# Revit family: HVAC_PTAC-Heat-Pump
name_source: partatom
category: Mechanical Equipment
units: mm (PartAtom-declared; Revit-internal decimal feet)

## family parameters
Classification Number = 23.75.70.21.21
Cut with Voids When Loaded = No
Host = Face
Maintain Annotation Orientation = No
Part Type = Normal
Room Calculation Point = No
Round Connector Dimension = Use Diameter
Shared = No

## types (2) — shared parameters
Assembly Code = D3050200
Cooling EER = 13
Default Elevation = 0' - 0"
Dehumidification Rate = 1.7 pts / hr
Electrical_Amperage = 0 A
Electrical_Frequency = 0 Hz
Electrical_Phase = 1
Heating = Yes
Heating COP = 4
Indoor Fan CFM = 250 - 409 CFM
Keynote = 23 81 00
Poles = 2
Power Factor = 0.96
SHR = 0.79
STC Rating = 29
Standards Conformance = UL  ;  ULc  ;  AHRI
Temperature Range = 60 - 85 F
Unit Depth = 0' - 7 1/16"
Unit Height = 1' - 4"
Unit Weight = 98
Unit Width = 3' - 6"
Vent Fan CFM = 38 CFM
zero-valued in all types: Expected Lifespan (Years), Maintenance Schedule (Months), Warranty Duration (Years)

## per-type parameters (varying)
| type | Cooling Amp Draw | Cooling Capacity | Description | Electrical_Voltage | Heating Amp Draw | Heating Capacity | MEP Apparent Power | Manufacturer | Model | Power Consumption_Cooling | Power Consumption_Heating | Type Comments | URL |
| 230V Base Model 7k Load | 2.5 FL - 13.5 LR | 2250.7 Btu/h |  | 21 V | 2.1 | 1965.4 Btu/h | 42 VA |  |  | 51 VA | 42 VA |  |  |
| 208V Base Model 7k Load | 2.7 FL - 13.5 LR | 2187.3 Btu/h | GE Zoneline Wall Mounted Heat Pump Commercial Air Conditioner - PTAC AZ65H07DAB as Specified | 19 V | 2.2 | 1933.7 Btu/h | 41 VA | GE Zoneline | AZ65H07DAB | 49 VA | 41 VA | Contact GE for up-to-date install requirements. | http://www.geappliances.com |

## geometry (parser evidence)
native form markers: Sweep x5
no freeform markers — native parametric forms only
